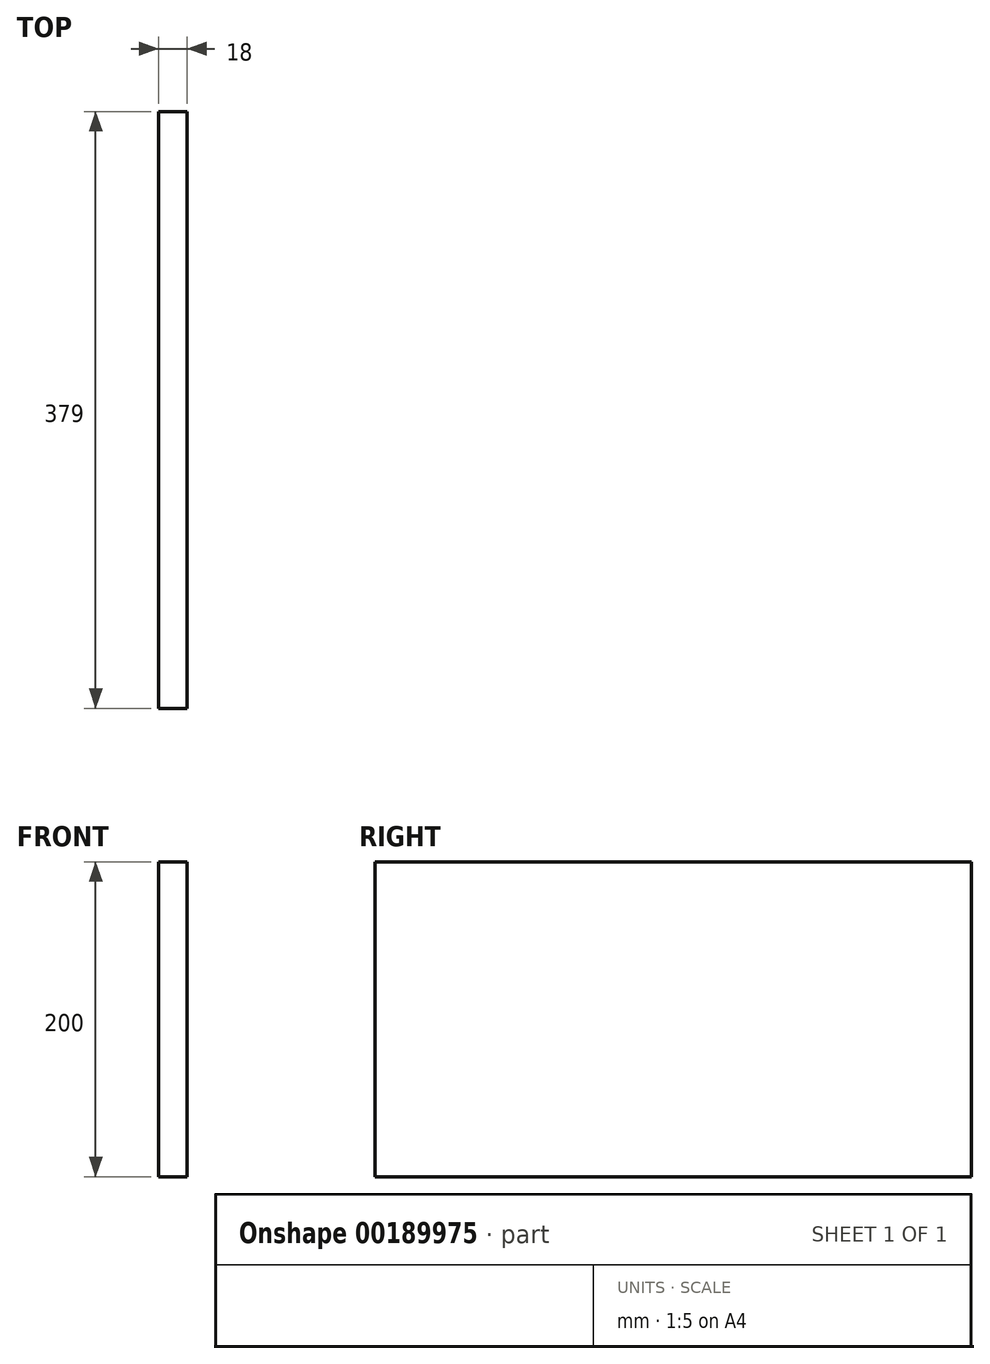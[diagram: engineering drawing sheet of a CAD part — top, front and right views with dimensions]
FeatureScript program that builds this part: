
annotation { "Feature Type Name" : "Feature", "Feature Type Description" : "" }
export const myFeature = defineFeature(function(context is Context, id is Id, definition is map)
    precondition{}
    {
        {
            var Q0;
            Q0=qCreatedBy(makeId("Right.planeOp"),FACE);
            var sketch = newSketch(context, id + "F0", { "sketchPlane" : qUnion([Q0])});
            skLineSegment(sketch, "E0.bottom", {"start": v(-288.94, -200) * mm, "end": v(90.06, -200) * mm});
            skLineSegment(sketch, "E0.top", {"start": v(-288.94, 0) * mm, "end": v(90.06, 0) * mm});
            skLineSegment(sketch, "E0.left", {"start": v(-288.94, -200) * mm, "end": v(-288.94, 0) * mm});
            skLineSegment(sketch, "E0.right", {"start": v(90.06, -200) * mm, "end": v(90.06, 0) * mm});
            skSolve(sketch);
        }
        {
            var Q0;
            Q0 = qSketchRegion(id + "F0", true);
            extrude(context, id + "F1", {"entities" : qUnion([Q0]), "depth" : 18 * mm});
        }
    });
